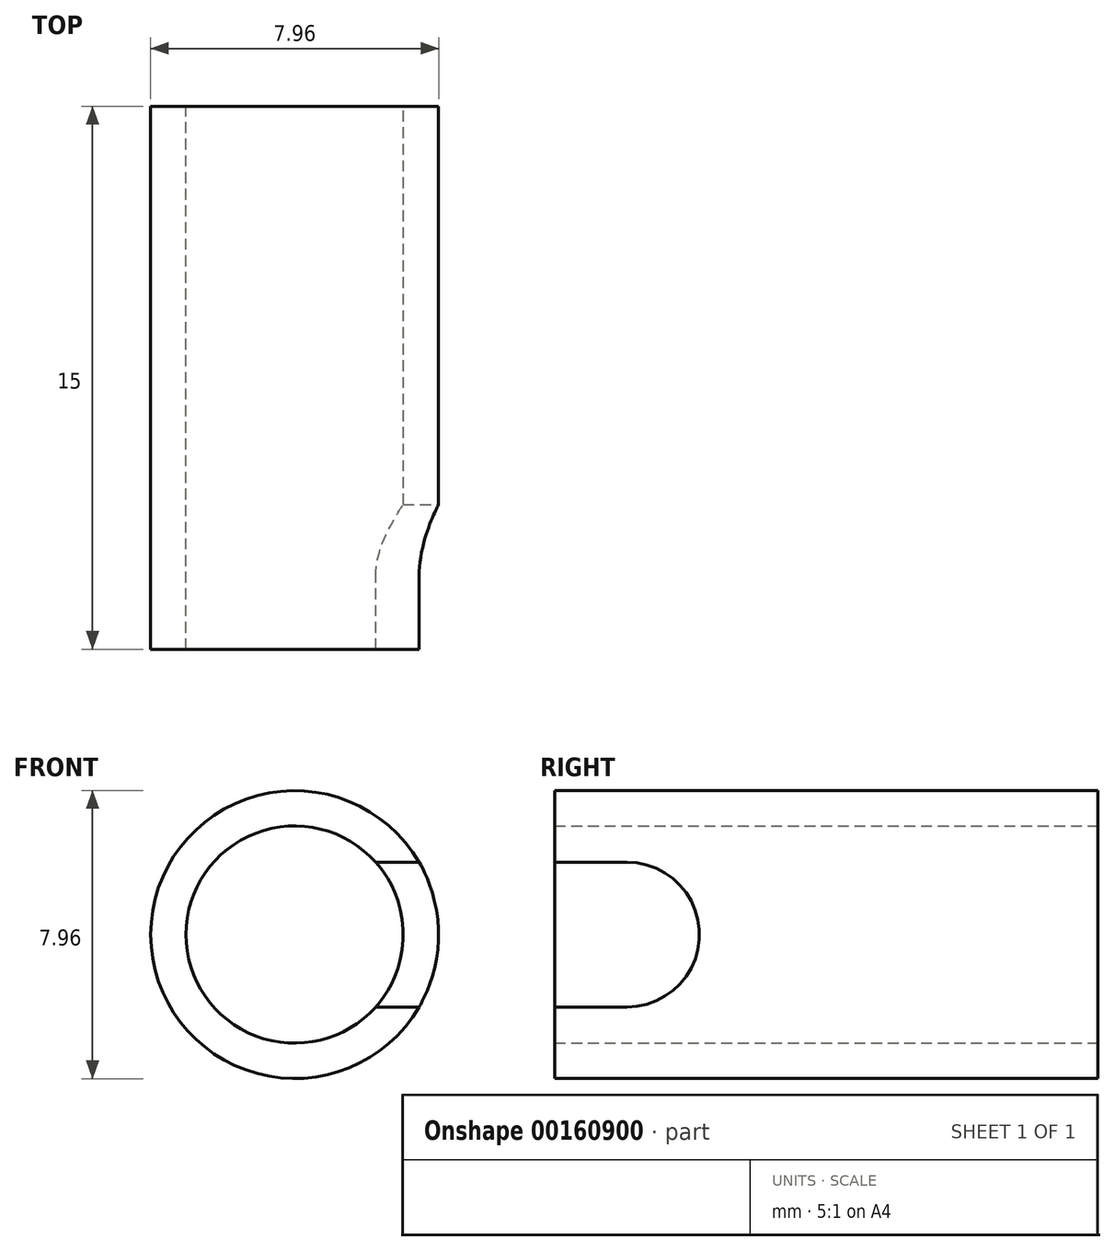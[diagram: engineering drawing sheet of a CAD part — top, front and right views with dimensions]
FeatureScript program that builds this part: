
annotation { "Feature Type Name" : "Feature", "Feature Type Description" : "" }
export const myFeature = defineFeature(function(context is Context, id is Id, definition is map)
    precondition{}
    {
        {
            var Q0;
            Q0=qCreatedBy(makeId("Front.planeOp"),FACE);
            var sketch = newSketch(context, id + "F0", { "sketchPlane" : qUnion([Q0])});
            skCircle(sketch, "E0", {"center": v(0, 0) * mm, "radius": 3.98 * mm});
            skCircle(sketch, "E1", {"center": v(0, 0) * mm, "radius": 3 * mm});
            skSolve(sketch);
        }
        {
            var Q0;
            Q0=makeQuery(id+"F0.imprint","IMPRINT",FACE,{"disambiguationData":[TD([[makeQuery(id+"F0.imprint","IMPRINT",EDGE,{"derivedFrom":sQuery(id+"F0.wireOp",EDGE,"E0")}),1.0]])]});
            extrude(context, id + "F1", {"entities" : qUnion([Q0]), "depth" : 15 * mm});
        }
        {
            var Q0;
            Q0=qCreatedBy(makeId("Right.planeOp"),FACE);
            cPlane(context, id + "F2", {"entities" : qUnion([Q0]), "cplaneType" : CPlaneType.OFFSET, "offset" : 3.98 * mm, "width" : 150 * mm, "height" : 150 * mm});
        }
        {
            var Q0;
            Q0=qCreatedBy(id+"F2.planeOp",FACE);
            var sketch = newSketch(context, id + "F3", { "sketchPlane" : qUnion([Q0])});
            skLineSegment(sketch, "E2.0", {"start": v(-15, -3.98) * mm, "end": v(-15, 3.98) * mm});
            skLineSegment(sketch, "E3", {"start": v(-15, 0) * mm, "end": v(3.76, 0) * mm, "construction": true});
            skArc(sketch, "E4", {"start": v(-13, -2) * mm, "mid": v(-11, 0) * mm, "end": v(-13, 2) * mm});
            skLineSegment(sketch, "E5", {"start": v(-13, 2) * mm, "end": v(-15, 2) * mm});
            skLineSegment(sketch, "E6", {"start": v(-13, -2) * mm, "end": v(-15, -2) * mm});
            skSolve(sketch);
        }
        {
            var Q0;
            Q0=makeQuery(id+"F3.imprint","IMPRINT",FACE,{"disambiguationData":[TD([[makeQuery(id+"F3.imprint","IMPRINT",EDGE,{"derivedFrom":sQuery(id+"F3.wireOp",EDGE,"E4")}),1.0]])]});
            extrude(context, id + "F4", {"entities" : qUnion([Q0]), "operationType" : NewBodyOperationType.REMOVE, "oppositeDirection" : true, "depth" : 3 * mm});
        }
    });
